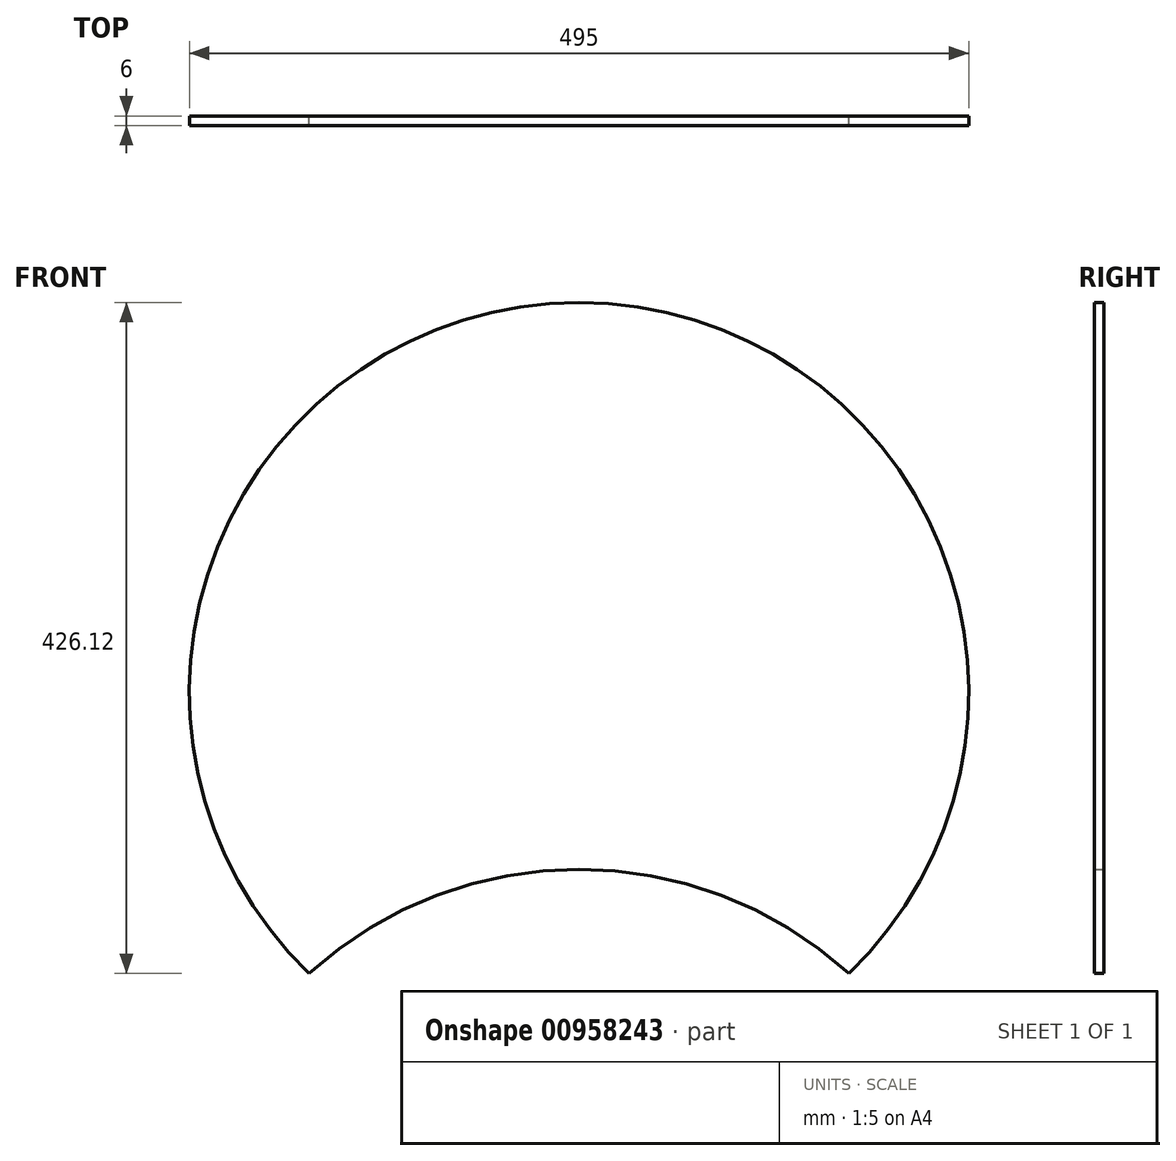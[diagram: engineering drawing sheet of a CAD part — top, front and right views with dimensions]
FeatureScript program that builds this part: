
annotation { "Feature Type Name" : "Feature", "Feature Type Description" : "" }
export const myFeature = defineFeature(function(context is Context, id is Id, definition is map)
    precondition{}
    {
        {
            var Q0;
            Q0=qCreatedBy(makeId("Front.planeOp"),FACE);
            var sketch = newSketch(context, id + "F0", { "sketchPlane" : qUnion([Q0])});
            skCircle(sketch, "E0", {"center": v(0, 0) * mm, "radius": 247.5 * mm});
            skArc(sketch, "E1", {"start": v(171.32, -178.62) * mm, "mid": v(0, -112.5) * mm, "end": v(-171.32, -178.62) * mm});
            skSolve(sketch);
        }
        {
            var Q0;
            {var subQ0=sQuery(id+"F0.wireOp",EDGE,"E1");Q0=makeQuery(id+"F0.imprint","IMPRINT",FACE,{"disambiguationData":[TD([[makeQuery(id+"F0.imprint","IMPRINT",EDGE,{"derivedFrom":subQ0}),-1.0]])]});}
            extrude(context, id + "F1", {"entities" : qUnion([Q0]), "depth" : 6 * mm, "offsetDistance" : 25.4 * mm});
        }
    });
